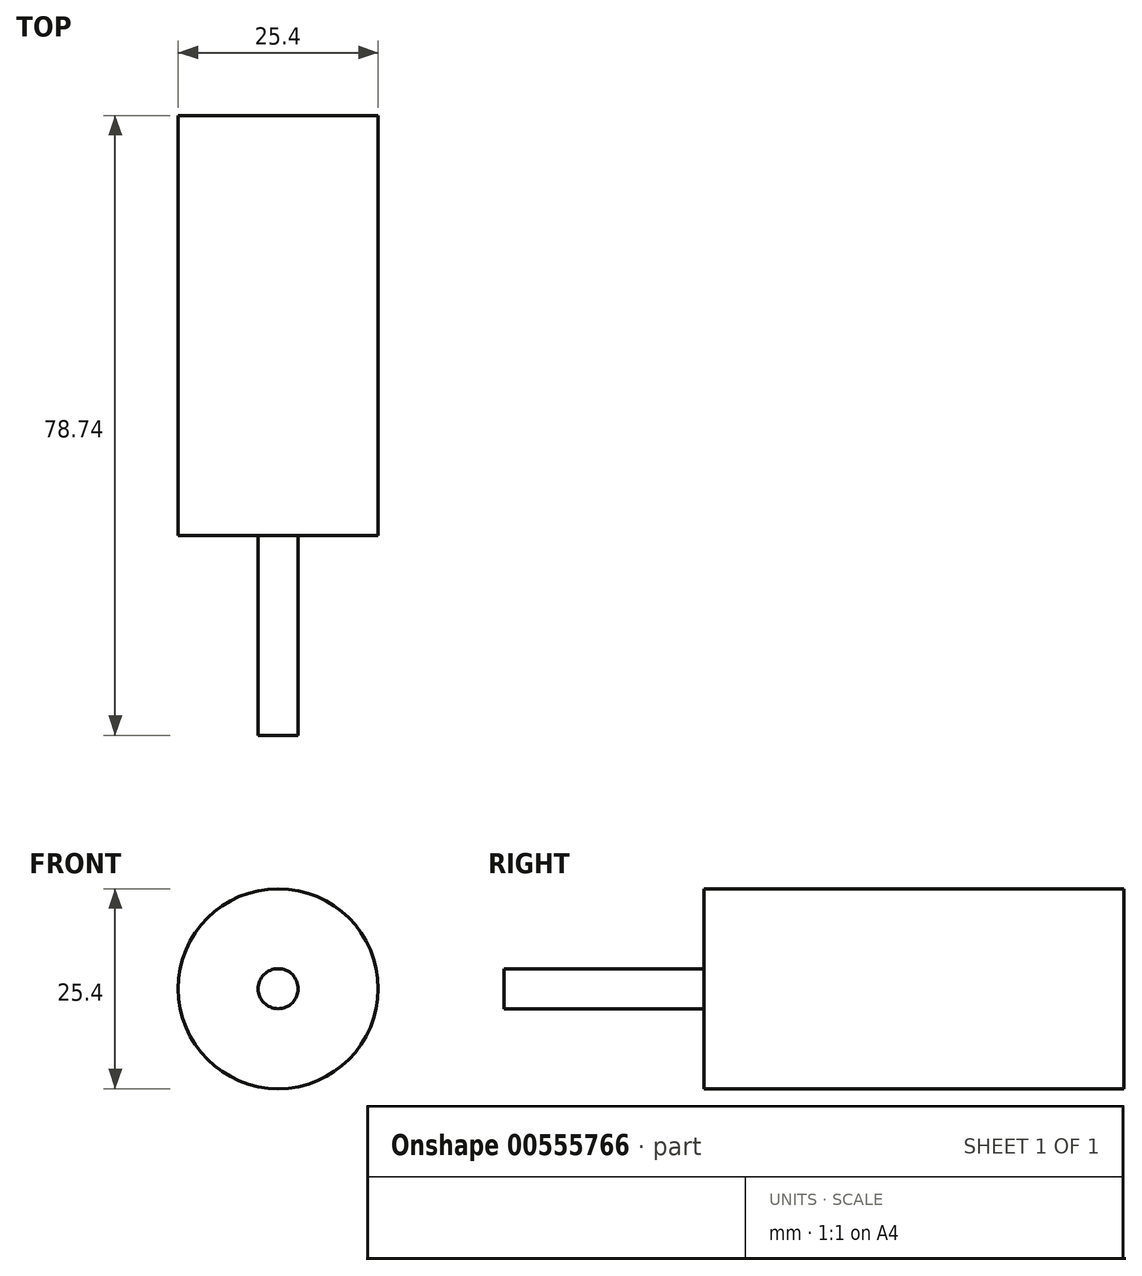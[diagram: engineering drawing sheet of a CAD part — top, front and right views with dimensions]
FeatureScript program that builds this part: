
annotation { "Feature Type Name" : "Feature", "Feature Type Description" : "" }
export const myFeature = defineFeature(function(context is Context, id is Id, definition is map)
    precondition{}
    {
        {
            var Q0;
            Q0=qCreatedBy(makeId("Front.planeOp"),FACE);
            var sketch = newSketch(context, id + "F0", { "sketchPlane" : qUnion([Q0])});
            skCircle(sketch, "E0", {"center": v(0, 0) * mm, "radius": 12.7 * mm});
            skSolve(sketch);
        }
        {
            var Q0;
            Q0 = qSketchRegion(id + "F0", true);
            extrude(context, id + "F1", {"entities" : qUnion([Q0]), "depth" : 53.34 * mm, "offsetDistance" : 25.4 * mm});
        }
        {
            var Q0;
            Q0=makeQuery(id+"F1.opExtrude","CAP_FACE",FACE,{"disambiguationData":[OSD([sQuery(id+"F0.wireOp",EDGE,"E0")])],"isStart":false});
            var sketch = newSketch(context, id + "F2", { "sketchPlane" : qUnion([Q0])});
            skCircle(sketch, "E1", {"center": v(0, 0) * mm, "radius": 2.54 * mm});
            skSolve(sketch);
        }
        {
            var Q0;
            Q0=makeQuery(id+"F2.imprint","IMPRINT",FACE,{"disambiguationData":[TD([[makeQuery(id+"F2.imprint","IMPRINT",EDGE,{"derivedFrom":sQuery(id+"F2.wireOp",EDGE,"E1")}),1.0]])]});
            extrude(context, id + "F3", {"entities" : qUnion([Q0]), "operationType" : NewBodyOperationType.ADD, "depth" : 25.4 * mm, "offsetDistance" : 25.4 * mm});
        }
    });
